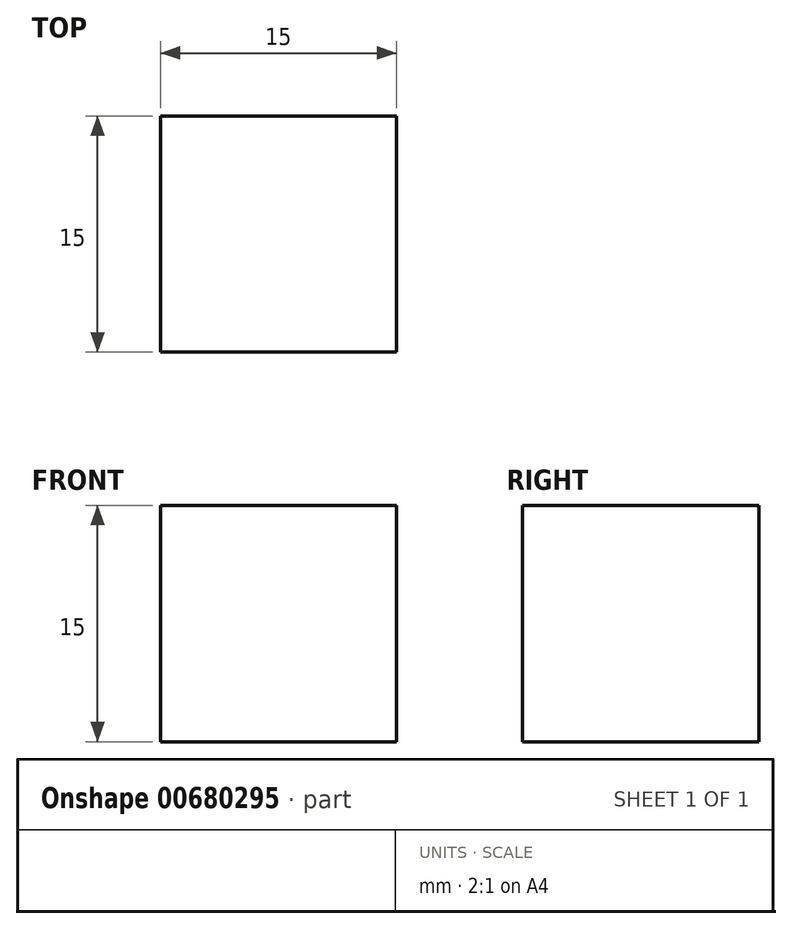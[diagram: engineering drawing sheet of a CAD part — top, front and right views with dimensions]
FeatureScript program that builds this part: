
annotation { "Feature Type Name" : "Feature", "Feature Type Description" : "" }
export const myFeature = defineFeature(function(context is Context, id is Id, definition is map)
    precondition{}
    {
        {
            var Q0;
            Q0=qCreatedBy(makeId("Top.planeOp"),FACE);
            var sketch = newSketch(context, id + "F0", { "sketchPlane" : qUnion([Q0])});
            skLineSegment(sketch, "E0.bottom", {"start": v(-7.5, -7.5) * mm, "end": v(7.5, -7.5) * mm});
            skLineSegment(sketch, "E0.top", {"start": v(-7.5, 7.5) * mm, "end": v(7.5, 7.5) * mm});
            skLineSegment(sketch, "E0.left", {"start": v(-7.5, -7.5) * mm, "end": v(-7.5, 7.5) * mm});
            skLineSegment(sketch, "E0.right", {"start": v(7.5, -7.5) * mm, "end": v(7.5, 7.5) * mm});
            skPoint(sketch, "E0.middle", {"position": v(0, 0) * mm});
            skSolve(sketch);
        }
        {
            var Q0;
            Q0=makeQuery(id+"F0.imprint","IMPRINT",FACE,{"disambiguationData":[TD([[makeQuery(id+"F0.imprint","IMPRINT",EDGE,{"derivedFrom":sQuery(id+"F0.wireOp",EDGE,"E0.bottom")}),1.0]])]});
            extrude(context, id + "F1", {"entities" : qUnion([Q0]), "depth" : 15 * mm, "offsetDistance" : 25 * mm});
        }
    });
